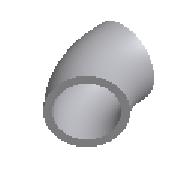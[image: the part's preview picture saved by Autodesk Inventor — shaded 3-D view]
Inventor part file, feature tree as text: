
AUTODESK INVENTOR PART (.ipt)
format: ipt  version: 2024.2 (Build 282272000, 272)  size: 177,664 bytes
history: native  units: mm (DEFAULTED — no unit token found)
features: other x4, sweep x1
ambient origin geometry x8: Origin, YZ Plane, XZ Plane, XY Plane, X Axis, Y Axis, Z Axis, Center Point
bodies: Solid1 (feature_tree)
feature tree (5):
  sweep  "Sweep1"
  other  "Work Point1"
  other  "Work Point2"
  other  "Work Axis1"
  other  "Work Axis2"
